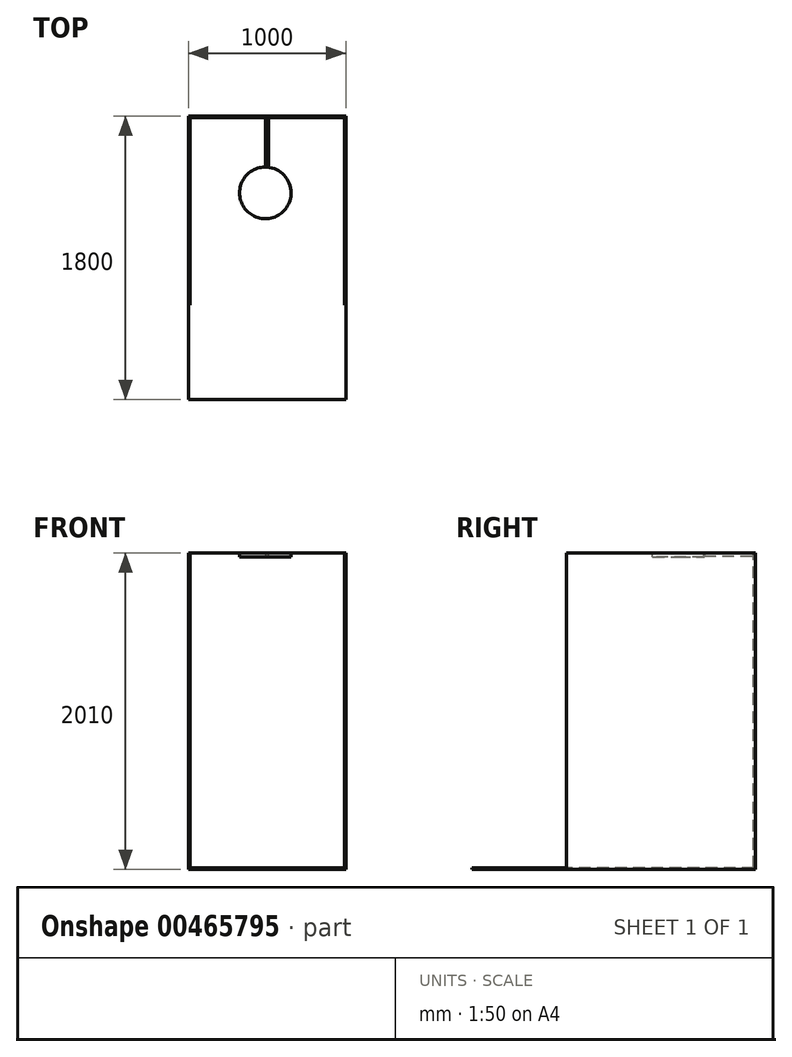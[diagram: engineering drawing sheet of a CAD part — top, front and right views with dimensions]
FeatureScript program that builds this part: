
annotation { "Feature Type Name" : "Feature", "Feature Type Description" : "" }
export const myFeature = defineFeature(function(context is Context, id is Id, definition is map)
    precondition{}
    {
        {
            var Q0;
            Q0=qCreatedBy(makeId("Top.planeOp"),FACE);
            var sketch = newSketch(context, id + "F0", { "sketchPlane" : qUnion([Q0])});
            skLineSegment(sketch, "E0.bottom", {"start": v(0, 0) * mm, "end": v(1000, 0) * mm});
            skLineSegment(sketch, "E0.top", {"start": v(0, -1800) * mm, "end": v(1000, -1800) * mm});
            skLineSegment(sketch, "E0.left", {"start": v(0, 0) * mm, "end": v(0, -1800) * mm});
            skLineSegment(sketch, "E0.right", {"start": v(1000, 0) * mm, "end": v(1000, -1800) * mm});
            skSolve(sketch);
        }
        {
            var Q0;
            Q0 = qSketchRegion(id + "F0", true);
            extrude(context, id + "F1", {"entities" : qUnion([Q0]), "depth" : 10 * mm});
        }
        {
            var Q0;
            Q0=makeQuery(id+"F1.opExtrude","CAP_FACE",FACE,{"disambiguationData":[OSD([sQuery(id+"F0.wireOp",EDGE,"E0.bottom"),sQuery(id+"F0.wireOp",EDGE,"E0.top"),sQuery(id+"F0.wireOp",EDGE,"E0.left"),sQuery(id+"F0.wireOp",EDGE,"E0.right")])],"isStart":false});
            var sketch = newSketch(context, id + "F2", { "sketchPlane" : qUnion([Q0])});
            skLineSegment(sketch, "E1.bottom", {"start": v(0, 0) * mm, "end": v(1000, 0) * mm});
            skLineSegment(sketch, "E1.top", {"start": v(0, -1200) * mm, "end": v(1000, -1200) * mm});
            skLineSegment(sketch, "E1.left", {"start": v(0, 0) * mm, "end": v(0, -1200) * mm});
            skLineSegment(sketch, "E1.right", {"start": v(1000, 0) * mm, "end": v(1000, -1200) * mm});
            skSolve(sketch);
        }
        {
            var Q0;
            Q0 = qSketchRegion(id + "F2", true);
            extrude(context, id + "F3", {"entities" : qUnion([Q0]), "operationType" : NewBodyOperationType.ADD, "depth" : 2000 * mm});
        }
        {
            var Q0;
            Q0=makeQuery(id+"F3.opExtrude","CAP_FACE",FACE,{"disambiguationData":[OSD([sQuery(id+"F2.wireOp",EDGE,"E1.bottom"),sQuery(id+"F2.wireOp",EDGE,"E1.top"),sQuery(id+"F2.wireOp",EDGE,"E1.left"),sQuery(id+"F2.wireOp",EDGE,"E1.right")])],"isStart":false});
            var sketch = newSketch(context, id + "F4", { "sketchPlane" : qUnion([Q0])});
            skLineSegment(sketch, "E2.bottom", {"start": v(10, -1200) * mm, "end": v(990, -1200) * mm});
            skLineSegment(sketch, "E2.top", {"start": v(10, -10) * mm, "end": v(990, -10) * mm});
            skLineSegment(sketch, "E2.left", {"start": v(10, -1200) * mm, "end": v(10, -10) * mm});
            skLineSegment(sketch, "E2.right", {"start": v(990, -1200) * mm, "end": v(990, -10) * mm});
            skSolve(sketch);
        }
        {
            var Q0;
            Q0 = qSketchRegion(id + "F4", true);
            var Q1;
            Q1=makeQuery(id+"F1.opExtrude","CAP_FACE",FACE,{"disambiguationData":[OSD([sQuery(id+"F0.wireOp",EDGE,"E0.bottom"),sQuery(id+"F0.wireOp",EDGE,"E0.top"),sQuery(id+"F0.wireOp",EDGE,"E0.left"),sQuery(id+"F0.wireOp",EDGE,"E0.right")])],"isStart":false});
            extrude(context, id + "F5", {"entities" : qUnion([Q0]), "operationType" : NewBodyOperationType.REMOVE, "endBound" : BoundingType.UP_TO_SURFACE, "oppositeDirection" : true, "endBoundEntityFace" : qUnion([Q1]), "depth" : 2000 * mm});
        }
        {
            var Q0;
            Q0=makeQuery(id+"F3.opExtrude","CAP_FACE",FACE,{"disambiguationData":[OSD([sQuery(id+"F2.wireOp",EDGE,"E1.bottom"),sQuery(id+"F2.wireOp",EDGE,"E1.top"),sQuery(id+"F2.wireOp",EDGE,"E1.left"),sQuery(id+"F2.wireOp",EDGE,"E1.right")])],"isStart":false});
            var sketch = newSketch(context, id + "F6", { "sketchPlane" : qUnion([Q0])});
            skCircle(sketch, "E3", {"center": v(488.6, -487.57) * mm, "radius": 163.76 * mm});
            skSolve(sketch);
        }
        {
            var Q0;
            Q0=makeQuery(id+"F3.boolean.opBoolean","MERGE",FACE,{"derivedFrom":[makeQuery(id+"F1.opExtrude","SWEPT_FACE",FACE,{"disambiguationData":[OSD([sQuery(id+"F0.wireOp",EDGE,"E0.bottom")])]}),makeQuery(id+"F3.opExtrude","SWEPT_FACE",FACE,{"disambiguationData":[OSD([sQuery(id+"F2.wireOp",EDGE,"E1.bottom")])]})]});
            var sketch = newSketch(context, id + "F7", { "sketchPlane" : qUnion([Q0])});
            skCircle(sketch, "E4", {"center": v(-500, 2000) * mm, "radius": 10 * mm});
            skSolve(sketch);
        }
        {
            var Q0;
            Q0 = qSketchRegion(id + "F7", true);
            extrude(context, id + "F8", {"entities" : qUnion([Q0]), "operationType" : NewBodyOperationType.ADD, "oppositeDirection" : true, "depth" : 500 * mm});
        }
        {
            var Q0;
            Q0 = qSketchRegion(id + "F6", true);
            extrude(context, id + "F9", {"entities" : qUnion([Q0]), "operationType" : NewBodyOperationType.ADD, "oppositeDirection" : true, "depth" : 25 * mm});
        }
    });
